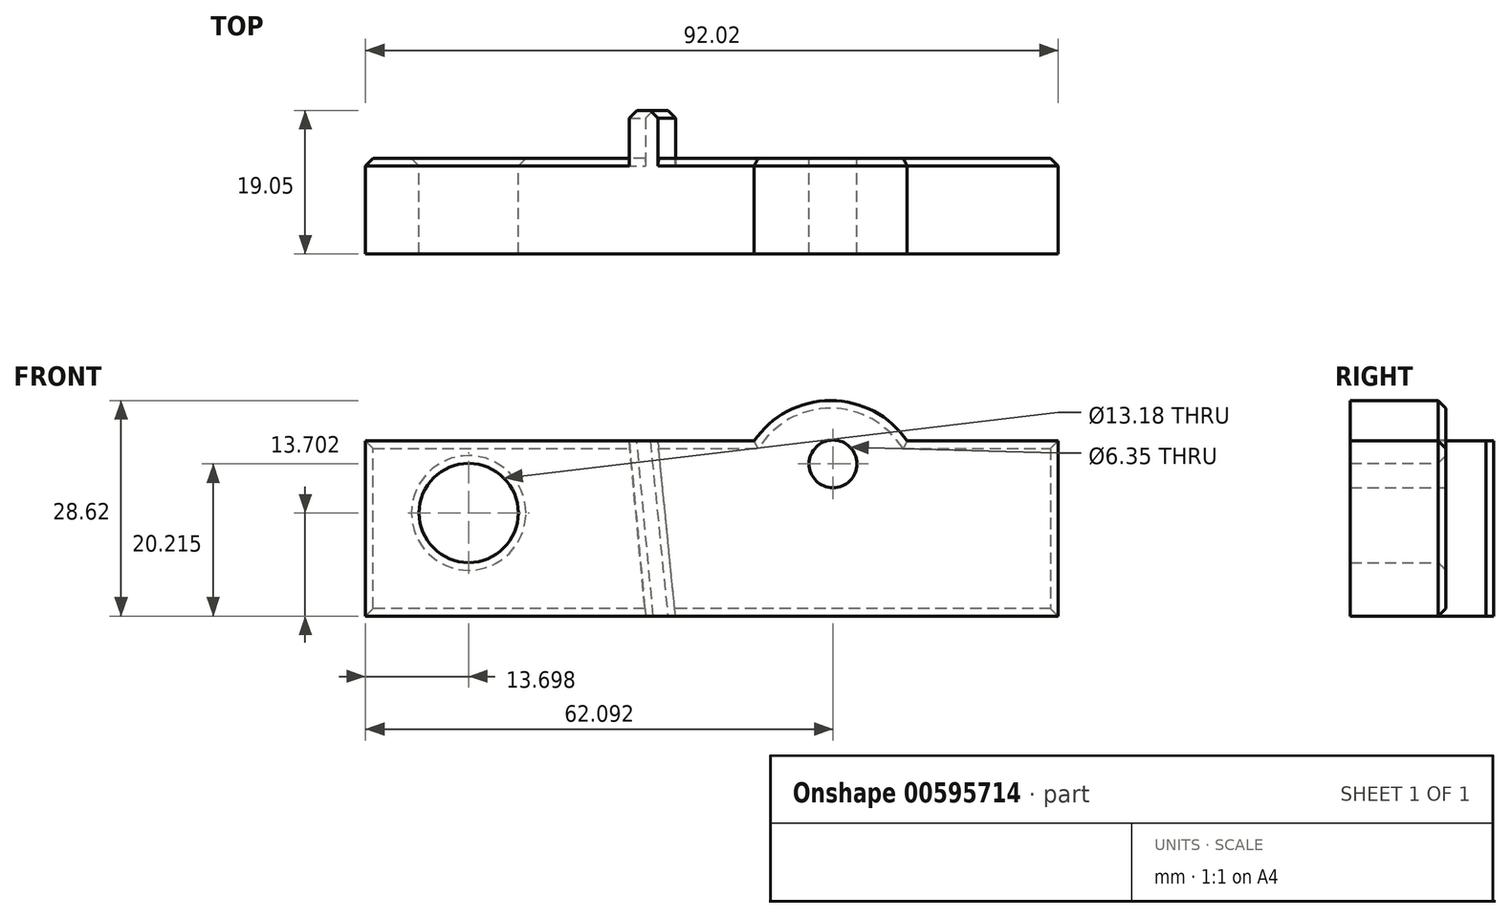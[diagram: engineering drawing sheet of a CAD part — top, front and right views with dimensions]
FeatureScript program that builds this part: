
annotation { "Feature Type Name" : "Feature", "Feature Type Description" : "" }
export const myFeature = defineFeature(function(context is Context, id is Id, definition is map)
    precondition{}
    {
        {
            var Q0;
            Q0=qCreatedBy(makeId("Front.planeOp"),FACE);
            var sketch = newSketch(context, id + "F0", { "sketchPlane" : qUnion([Q0])});
            skLineSegment(sketch, "E0.bottom", {"start": v(-45.62, 26.1) * mm, "end": v(46.4, 26.1) * mm});
            skLineSegment(sketch, "E0.top", {"start": v(-45.62, 2.84) * mm, "end": v(46.4, 2.84) * mm});
            skLineSegment(sketch, "E0.left", {"start": v(-45.62, 26.1) * mm, "end": v(-45.62, 2.84) * mm});
            skLineSegment(sketch, "E0.right", {"start": v(46.4, 26.1) * mm, "end": v(46.4, 2.84) * mm});
            skCircle(sketch, "E1", {"center": v(16.15, 19.13) * mm, "radius": 12.33 * mm});
            skCircle(sketch, "E2", {"center": v(-31.92, 16.54) * mm, "radius": 6.59 * mm});
            skSolve(sketch);
        }
        {
            var Q0;
            Q0 = qSketchRegion(id + "F0", true);
            extrude(context, id + "F1", {"entities" : qUnion([Q0]), "depth" : 12.7 * mm, "offsetDistance" : 25.4 * mm});
        }
        {
            var Q0;
            Q0=makeQuery(id+"F1.opExtrude","CAP_FACE",FACE,{"disambiguationData":[OSD([sQuery(id+"F0.wireOp",EDGE,"E0.bottom"),sQuery(id+"F0.wireOp",EDGE,"E0.top"),sQuery(id+"F0.wireOp",EDGE,"E0.left"),sQuery(id+"F0.wireOp",EDGE,"E0.right"),sQuery(id+"F0.wireOp",EDGE,"E1"),sQuery(id+"F0.wireOp",EDGE,"E2")])],"isStart":true});
            var sketch = newSketch(context, id + "F2", { "sketchPlane" : qUnion([Q0])});
            skLineSegment(sketch, "E3", {"start": v(4.45, 2.84) * mm, "end": v(6.79, 26.1) * mm});
            skLineSegment(sketch, "E4", {"start": v(8.42, 2.84) * mm, "end": v(10.6, 26.1) * mm});
            skSolve(sketch);
        }
        {
            var Q0;
            {var subQ0=sQuery(id+"F2.wireOp",EDGE,"E3");Q0=makeQuery(id+"F2.imprint","IMPRINT",FACE,{"disambiguationData":[TD([[makeQuery(id+"F2.imprint","IMPRINT",EDGE,{"derivedFrom":subQ0}),-1.0]])]});}
            extrude(context, id + "F3", {"entities" : qUnion([Q0]), "operationType" : NewBodyOperationType.ADD, "depth" : 6.35 * mm, "offsetDistance" : 25.4 * mm});
        }
        {
            var Q0;
            Q0=makeQuery(id+"F3.opExtrude","CAP_EDGE",EDGE,{"disambiguationData":[OSD([sQuery(id+"F2.wireOp",EDGE,"E4")])],"isStart":false});
            var Q1;
            Q1=makeQuery(id+"F3.opExtrude","CAP_EDGE",EDGE,{"disambiguationData":[OSD([sQuery(id+"F2.wireOp",EDGE,"E3")])],"isStart":false});
            var Q2;
            {var subQ0=sQuery(id+"F0.wireOp",EDGE,"E0.right");var subQ1=sQuery(id+"F0.wireOp",EDGE,"E0.top");Q2=makeQuery(id+"F3.boolean.opBoolean","SPLIT",EDGE,{"disambiguationData":[TD([makeQuery(id+"F1.opExtrude","SWEPT_FACE",FACE,{"disambiguationData":[OSD([subQ0])]})])],"derivedFrom":makeQuery(id+"F1.opExtrude","CAP_EDGE",EDGE,{"disambiguationData":[OSD([subQ1])],"isStart":true})});}
            var Q3;
            {var subQ0=sQuery(id+"F0.wireOp",EDGE,"E0.left");var subQ1=sQuery(id+"F0.wireOp",EDGE,"E0.top");Q3=makeQuery(id+"F3.boolean.opBoolean","SPLIT",EDGE,{"disambiguationData":[TD([makeQuery(id+"F1.opExtrude","SWEPT_FACE",FACE,{"disambiguationData":[OSD([subQ0])]})])],"derivedFrom":makeQuery(id+"F1.opExtrude","CAP_EDGE",EDGE,{"disambiguationData":[OSD([subQ1])],"isStart":true})});}
            var Q4;
            Q4=makeQuery(id+"F1.opExtrude","CAP_EDGE",EDGE,{"disambiguationData":[OSD([sQuery(id+"F0.wireOp",EDGE,"E2")])],"isStart":true});
            var Q5;
            Q5=makeQuery(id+"F1.opExtrude","CAP_EDGE",EDGE,{"disambiguationData":[OSD([sQuery(id+"F0.wireOp",EDGE,"E1")])],"isStart":true});
            var Q6;
            {var subQ0=sQuery(id+"F0.wireOp",EDGE,"E1");var subQ1=sQuery(id+"F0.wireOp",EDGE,"E0.left");var subQ2=sQuery(id+"F0.wireOp",EDGE,"E0.bottom");var subQ3=makeQuery(id+"F0.imprint","IMPRINT",EDGE,{"disambiguationData":[TD([[makeQuery(id+"F0.imprint","INTERSECT",VERTEX,{"derivedFrom":[subQ2,subQ1]}),-1.0]])],"derivedFrom":subQ2});Q6=makeQuery(id+"F3.boolean.opBoolean","SPLIT",EDGE,{"disambiguationData":[TD([makeQuery(id+"F1.opExtrude","SWEPT_FACE",FACE,{"disambiguationData":[OSD([subQ0])]})])],"derivedFrom":makeQuery(id+"F1.opExtrude","CAP_EDGE",EDGE,{"disambiguationData":[OSD([subQ2]),TDD([subQ3])],"isStart":true})});}
            var Q7;
            {var subQ1=sQuery(id+"F0.wireOp",EDGE,"E0.left");var subQ2=sQuery(id+"F0.wireOp",EDGE,"E0.bottom");var subQ3=makeQuery(id+"F0.imprint","IMPRINT",EDGE,{"disambiguationData":[TD([[makeQuery(id+"F0.imprint","INTERSECT",VERTEX,{"derivedFrom":[subQ2,subQ1]}),-1.0]])],"derivedFrom":subQ2});Q7=makeQuery(id+"F3.boolean.opBoolean","SPLIT",EDGE,{"disambiguationData":[TD([makeQuery(id+"F1.opExtrude","SWEPT_FACE",FACE,{"disambiguationData":[OSD([subQ1])]})])],"derivedFrom":makeQuery(id+"F1.opExtrude","CAP_EDGE",EDGE,{"disambiguationData":[OSD([subQ2]),TDD([subQ3])],"isStart":true})});}
            var Q8;
            Q8=makeQuery(id+"F1.opExtrude","CAP_EDGE",EDGE,{"disambiguationData":[OSD([sQuery(id+"F0.wireOp",EDGE,"E0.left")])],"isStart":true});
            var Q9;
            Q9=makeQuery(id+"F1.opExtrude","CAP_EDGE",EDGE,{"disambiguationData":[OSD([sQuery(id+"F0.wireOp",EDGE,"E0.right")])],"isStart":true});
            var Q10;
            {var subQ0=sQuery(id+"F0.wireOp",EDGE,"E0.bottom");Q10=makeQuery(id+"F1.opExtrude","CAP_EDGE",EDGE,{"disambiguationData":[OSD([subQ0]),TDD([makeQuery(id+"F0.imprint","IMPRINT",EDGE,{"disambiguationData":[TD([[makeQuery(id+"F0.imprint","INTERSECT",VERTEX,{"derivedFrom":[subQ0,sQuery(id+"F0.wireOp",EDGE,"E0.right")]}),1.0]])],"derivedFrom":subQ0})])],"isStart":true});}
            chamfer(context, id + "F4", {"entities" : qUnion([Q0, Q1, Q2, Q3, Q4, Q5, Q6, Q7, Q8, Q9, Q10]), "width" : 1.02 * mm, "tangentPropagation" : true});
        }
        {
            var Q0;
            {var subQ0=sQuery(id+"F0.wireOp",EDGE,"E0.right");var subQ1=sQuery(id+"F0.wireOp",EDGE,"E0.top");var subQ2=sQuery(id+"F0.wireOp",EDGE,"E0.bottom");var subQ3=sQuery(id+"F0.wireOp",EDGE,"E1");var subQ4=sQuery(id+"F0.wireOp",EDGE,"E0.left");Q0=makeQuery(id+"F3.boolean.opBoolean","SPLIT",FACE,{"disambiguationData":[TD([makeQuery(id+"F1.opExtrude","SWEPT_FACE",FACE,{"disambiguationData":[OSD([subQ0])]})])],"derivedFrom":makeQuery(id+"F1.opExtrude","CAP_FACE",FACE,{"disambiguationData":[OSD([subQ2,subQ1,subQ4,subQ0,subQ3,sQuery(id+"F0.wireOp",EDGE,"E2")])],"isStart":true})});}
            var sketch = newSketch(context, id + "F5", { "sketchPlane" : qUnion([Q0])});
            skCircle(sketch, "E5", {"center": v(-16.47, 23.05) * mm, "radius": 5.8 * mm});
            skSolve(sketch);
        }
        {
            var Q0;
            Q0=sQuery(id+"F5.wireOp",VERTEX,"E5.center");
            var Q1;
            Q1=makeQuery(id+"F1.opExtrude","SWEPT_BODY",BODY,{"disambiguationData":[OSD([sQuery(id+"F0.wireOp",EDGE,"E0.bottom"),sQuery(id+"F0.wireOp",EDGE,"E0.top"),sQuery(id+"F0.wireOp",EDGE,"E0.left"),sQuery(id+"F0.wireOp",EDGE,"E0.right"),sQuery(id+"F0.wireOp",EDGE,"E1"),sQuery(id+"F0.wireOp",EDGE,"E2")])]});
            hole(context, id + "F6", {"style" : HoleStyle.SIMPLE, "endStyle" : HoleEndStyle.THROUGH, "holeDiameter" : 6.35 * mm, "majorDiameter" : 6.35 * mm, "isTappedThrough" : true, "tappedDepth" : 12.7 * mm, "tapClearance" : 3, "locations" : qUnion([Q0]), "scope" : qUnion([Q1])});
        }
    });
